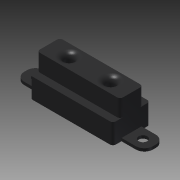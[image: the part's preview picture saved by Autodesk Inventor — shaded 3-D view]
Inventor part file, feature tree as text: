
AUTODESK INVENTOR PART (.ipt)
format: ipt  version: 2015 (Build 190159000, 159)  size: 207,872 bytes
history: native  units: mm
features: sketch x8, extrude x6, fillet x3, other x1, hole x1
ambient origin geometry x8: Origin, YZ Plane, XZ Plane, XY Plane, X Axis, Y Axis, Z Axis, Center Point
bodies: Body1 (feature_tree)
feature tree (19):
  other  "ソリッド1"
  extrude  "押し出し1"  Depth=45.0mm
  extrude  "押し出し2"  Depth=13.0mm
  extrude  "押し出し3"  Depth=1.0mm TaperAngle=0.0deg
  sketch  "スケッチ5"
  extrude  "押し出し4"  Depth=29.0mm
  fillet  "フィレット1"  Radius=13.0mm
  hole  "穴1"  [1 undecoded]
  fillet  "フィレット2"  Radius=29.0mm
  extrude  "押し出し5"  Depth=8.0mm
  extrude  "押し出し6"  Depth=6.0mm TaperAngle=0.0deg
  fillet  "フィレット3"  Radius=8.0mm
  sketch  "スケッチ1"
  sketch  "スケッチ2"
  sketch  "スケッチ4"
  sketch  "スケッチ6"
  sketch  "スケッチ7"
  sketch  "スケッチ8"
  sketch  "スケッチ9"
note: 1 required parameter value undecoded (feature->parameter linkage not recoverable at this tier; creation-order binding heuristic only, values carry confidence <= 0.55)
